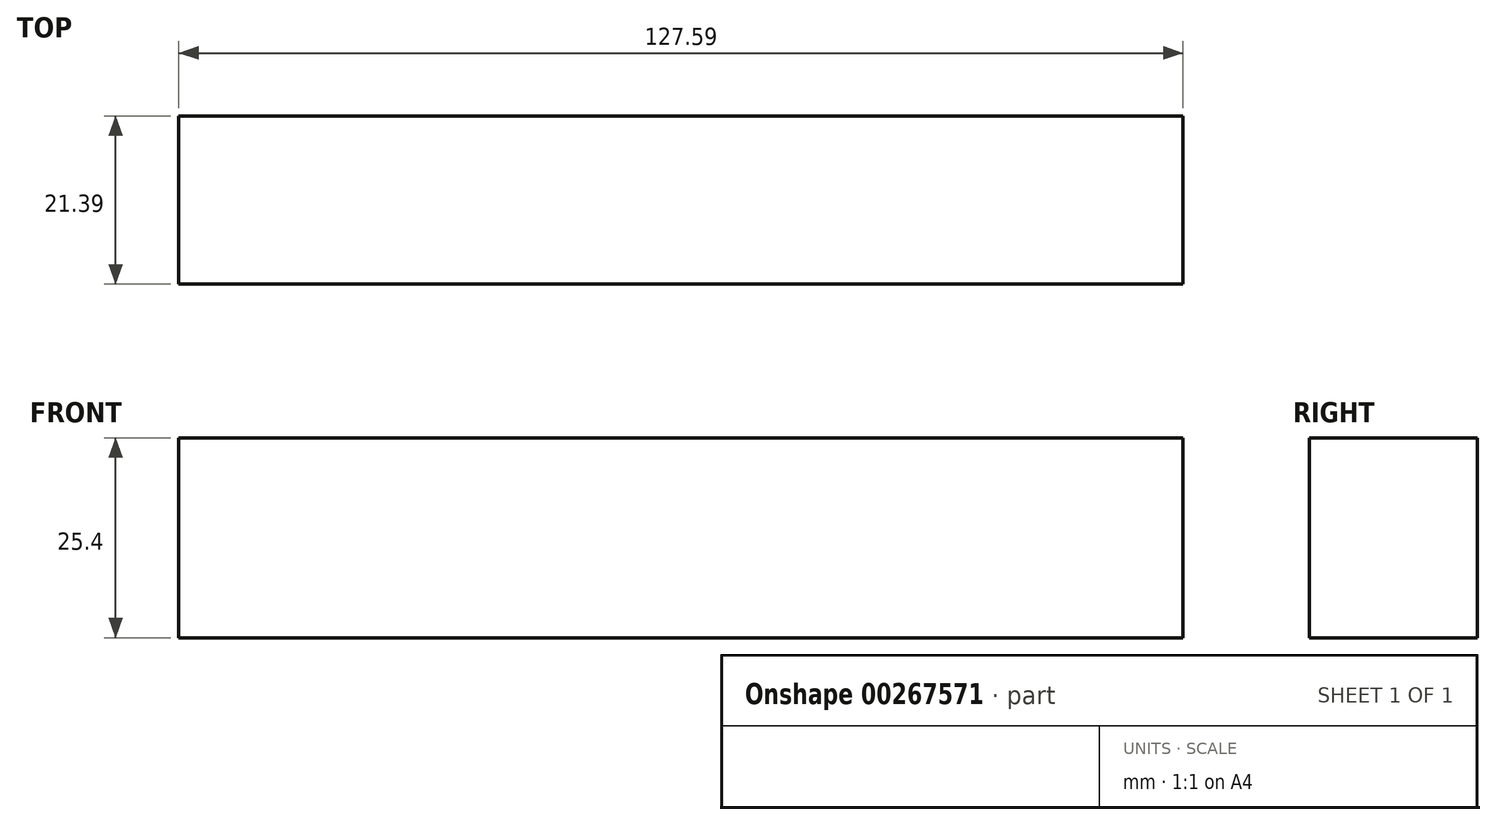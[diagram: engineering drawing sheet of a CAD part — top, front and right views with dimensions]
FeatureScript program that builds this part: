
annotation { "Feature Type Name" : "Feature", "Feature Type Description" : "" }
export const myFeature = defineFeature(function(context is Context, id is Id, definition is map)
    precondition{}
    {
        {
            var Q0;
            Q0=qCreatedBy(makeId("Top.planeOp"),FACE);
            var sketch = newSketch(context, id + "F0", { "sketchPlane" : qUnion([Q0])});
            skLineSegment(sketch, "E0.bottom", {"start": v(-61.56, 10.46) * mm, "end": v(66.03, 10.46) * mm});
            skLineSegment(sketch, "E0.top", {"start": v(-61.56, -10.93) * mm, "end": v(66.03, -10.93) * mm});
            skLineSegment(sketch, "E0.left", {"start": v(-61.56, 10.46) * mm, "end": v(-61.56, -10.93) * mm});
            skLineSegment(sketch, "E0.right", {"start": v(66.03, 10.46) * mm, "end": v(66.03, -10.93) * mm});
            skSolve(sketch);
        }
        {
            var Q0;
            Q0=makeQuery(id+"F0.imprint","IMPRINT",FACE,{"disambiguationData":[TD([[makeQuery(id+"F0.imprint","IMPRINT",EDGE,{"derivedFrom":sQuery(id+"F0.wireOp",EDGE,"E0.bottom")}),-1.0]])]});
            extrude(context, id + "F1", {"entities" : qUnion([Q0]), "depth" : 25.4 * mm});
        }
    });
